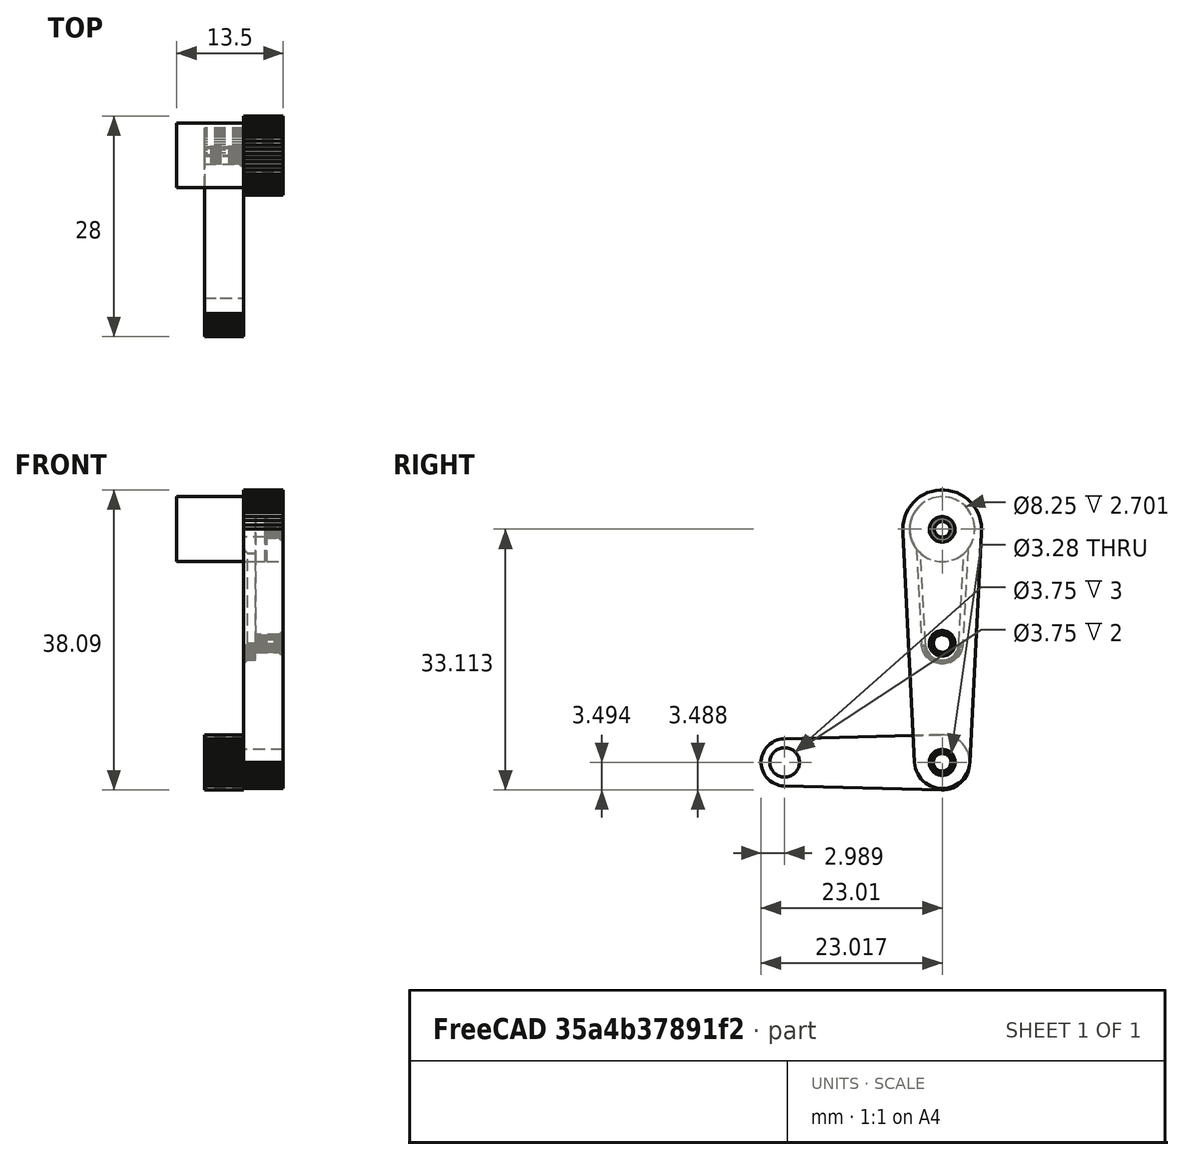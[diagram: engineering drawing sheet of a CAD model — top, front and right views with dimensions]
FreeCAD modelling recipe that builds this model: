
FCSTD DOCUMENT  (FreeCAD 1.0R39109 (Git))
Label: servo-trigger
License: All rights reserved
LicenseURL: https://en.wikipedia.org/wiki/All_rights_reserved
objects: Part::Extrusion×11, Sketcher::SketchObject×7, Part::Cut×6, Mesh::Feature×4, Part::Feature×4, Part::Refine×2, Part::Fuse×2
note: 39 computed .brp shape members not serialized (recipe doc carries the construction recipe); baked Part::Feature solids carry a one-line shape summary decoded from their .brp

FEATURE [Mesh::Feature] trigger_extension  label="trigger-extension"
FEATURE [Mesh::Feature] servo_trigger  label="servo-trigger"
FEATURE [Part::Feature] servo_trigger001
  shape: bbox 5 x 10 x 37.92 mm, 1666 faces, 0 solids (baked)
FEATURE [Part::Refine] servo_trigger002
  Source = -> servo_trigger001
FEATURE [Sketcher::SketchObject] Sketch
  ArcFitTolerance = 1e-06
  AttachmentSupport = -> [servo_trigger002]
  ExternalGeometry = -> [servo_trigger002]
  FullyConstrained = true
  MakeInternals = false
  MapMode = 5
  Placement = pos=(-3,0,0) rot=(0.57735,-0.57735,-0.57735;2.0944rad)
  sketch-geometry (3):
    g0: Circle CenterX=-59.0871 CenterY=190.492 CenterZ=0 NormalX=0 NormalY=0 NormalZ=1 AngleXU=0 Radius=4.125
    g1: LineSegment [constr] StartX=-59.0089 StartY=191.604 StartZ=0 EndX=-59.1307 EndY=189.357 EndZ=0
    g2: LineSegment [constr] StartX=-60.1685 StartY=190.722 StartZ=0 EndX=-58.0037 EndY=190.121 EndZ=0
  constraints (7):
    c: Diameter(g0) = 8.25
    c: Coincident(g1,g-25)
    c: Coincident(g1,g-41)
    c: Coincident(g2,g-33)
    c: Coincident(g2,g-16)
    c: Block(g2)
    c: Block(g0)
FEATURE [Part::Extrusion] Extrude
  Base = -> Sketch
  Dir = (-1,0,0)
  DirMode = 2
  FaceMakerClass = Part::FaceMakerBullseye
  FaceMakerMode = 3
  LengthFwd = 10
  LengthRev = 0
  Solid = true
  Symmetric = false
FEATURE [Part::Extrusion] Extrude001
  Base = -> Sketch
  Dir = (-1,0,0)
  DirMode = 2
  FaceMakerClass = Part::FaceMakerBullseye
  FaceMakerMode = 3
  LengthFwd = 10
  LengthRev = 1.5
  Solid = true
  Symmetric = false
FEATURE [Part::Cut] Cut
  Base = -> servo_trigger002
  Tool = -> Extrude001
FEATURE [Part::Extrusion] Extrude002
  Base = -> Sketch
  Dir = (-1,0,0)
  DirMode = 2
  FaceMakerClass = Part::FaceMakerBullseye
  FaceMakerMode = 3
  LengthFwd = 0
  LengthRev = 2
  Placement = pos=(1.4,0,0) rot=(0,0,1;0rad)
  Solid = true
  Symmetric = false
FEATURE [Sketcher::SketchObject] Sketch001
  ArcFitTolerance = 1e-06
  AttachmentSupport = -> [Cut]
  FullyConstrained = true
  MakeInternals = false
  MapMode = 5
  Placement = pos=(0.5,0,0) rot=(0.57735,0.57735,0.57735;2.0944rad)
  sketch-geometry (2):
    g0: Circle CenterX=59.0881 CenterY=190.477 CenterZ=0 NormalX=0 NormalY=0 NormalZ=1 AngleXU=0 Radius=1
    g1: Circle [constr] CenterX=59.0754 CenterY=190.477 CenterZ=0 NormalX=0 NormalY=0 NormalZ=1 AngleXU=0 Radius=1.61528
  constraints (3):
    c: Diameter(g0) = 2
    c: Block(g1)
    c: Block(g0)
FEATURE [Part::Extrusion] Extrude003
  Base = -> Sketch001
  Dir = (1,0,0)
  DirMode = 2
  FaceMakerClass = Part::FaceMakerBullseye
  FaceMakerMode = 3
  LengthFwd = 0
  LengthRev = 5
  Solid = true
  Symmetric = false
FEATURE [Part::Feature] servo_trigger003_solid  label="servo_trigger003 (Solid)"
  shape: bbox 5 x 10 x 37.92 mm, 1110 faces (baked)
FEATURE [Part::Extrusion] Extrude004
  Base = -> Sketch
  Dir = (-1,0,0)
  DirMode = 2
  FaceMakerClass = Part::FaceMakerBullseye
  FaceMakerMode = 3
  LengthFwd = 10
  LengthRev = 1.2
  Solid = true
  Symmetric = false
FEATURE [Part::Cut] Cut001
  Base = -> servo_trigger003_solid
  Tool = -> Extrude004
FEATURE [Sketcher::SketchObject] Sketch002
  ArcFitTolerance = 1e-06
  AttachmentSupport = -> [Cut001]
  FullyConstrained = true
  MakeInternals = false
  MapMode = 5
  Placement = pos=(0.5,0,0) rot=(0.57735,0.57735,0.57735;2.0944rad)
  sketch-geometry (1):
    g0: Circle CenterX=59.0801 CenterY=160.874 CenterZ=0 NormalX=0 NormalY=0 NormalZ=1 AngleXU=0 Radius=1.64167
  constraints (1):
    c: Block(g0)
FEATURE [Part::Extrusion] Extrude006
  Base = -> Sketch002
  Dir = (1,0,0)
  DirMode = 2
  FaceMakerClass = Part::FaceMakerBullseye
  FaceMakerMode = 3
  LengthFwd = 0
  LengthRev = 5
  Solid = true
  Symmetric = false
FEATURE [Part::Fuse] Fusion
  Base = -> Cut001
  Tool = -> Extrude006
FEATURE [Part::Extrusion] Extrude007
  Base = -> Sketch002
  Dir = (1,0,0)
  DirMode = 2
  FaceMakerClass = Part::FaceMakerBullseye
  FaceMakerMode = 3
  LengthFwd = 0
  LengthRev = 5
  Solid = true
  Symmetric = false
FEATURE [Part::Cut] Cut002
  Base = -> Fusion
  Tool = -> Extrude007
FEATURE [Part::Feature] trigger_extension001
  shape: bbox 5 x 26.5 x 6.998 mm, 904 faces, 0 solids (baked)
FEATURE [Part::Refine] trigger_extension002
  Source = -> trigger_extension001
FEATURE [Part::Feature] trigger_extension002_solid  label="trigger_extension002 (Solid)"
  shape: bbox 5 x 26.5 x 6.998 mm, 529 faces (baked)
FEATURE [Sketcher::SketchObject] Sketch003
  ArcFitTolerance = 1e-06
  AttachmentSupport = -> [trigger_extension002_solid]
  FullyConstrained = true
  MakeInternals = false
  MapMode = 5
  Placement = pos=(-9.5,0,0) rot=(0.57735,-0.57735,-0.57735;2.0944rad)
  sketch-geometry (1):
    g0: Circle CenterX=-39.0698 CenterY=160.877 CenterZ=0 NormalX=0 NormalY=0 NormalZ=1 AngleXU=0 Radius=2.225
  constraints (2):
    c: Diameter(g0) = 4.45
    c: Block(g0)
FEATURE [Part::Extrusion] Extrude008
  Base = -> Sketch003
  Dir = (-1,0,0)
  DirMode = 2
  FaceMakerClass = Part::FaceMakerBullseye
  FaceMakerMode = 3
  LengthFwd = 0
  LengthRev = 5
  Solid = true
  Symmetric = false
FEATURE [Part::Fuse] Fusion001
  Base = -> trigger_extension002_solid
  Tool = -> Extrude008
FEATURE [Sketcher::SketchObject] Sketch004
  ArcFitTolerance = 1e-06
  AttachmentSupport = -> [Fusion001]
  FullyConstrained = true
  MakeInternals = false
  MapMode = 5
  Placement = pos=(-9.5,0,0) rot=(0.57735,-0.57735,-0.57735;2.0944rad)
  sketch-geometry (2):
    g0: Circle [constr] CenterX=-39.0641 CenterY=160.873 CenterZ=0 NormalX=0 NormalY=0 NormalZ=1 AngleXU=0 Radius=2.225
    g1: Circle CenterX=-39.0639 CenterY=160.874 CenterZ=0 NormalX=0 NormalY=0 NormalZ=1 AngleXU=0 Radius=1.5
  constraints (4):
    c: Diameter(g0) = 4.45
    c: Diameter(g1) = 3
    c: Block(g0)
    c: Block(g1)
FEATURE [Part::Extrusion] Extrude009
  Base = -> Sketch004
  Dir = (-1,0,0)
  DirMode = 2
  FaceMakerClass = Part::FaceMakerBullseye
  FaceMakerMode = 3
  LengthFwd = 0
  LengthRev = 3
  Placement = pos=(2.1,0,0) rot=(0,0,1;0rad)
  Solid = true
  Symmetric = false
FEATURE [Part::Cut] Cut003
  Base = -> Fusion001
  Tool = -> Extrude009
FEATURE [Mesh::Feature] Mesh  label="servo-trigger001"
FEATURE [Sketcher::SketchObject] Sketch005
  ArcFitTolerance = 1e-06
  AttachmentSupport = -> [Cut003]
  FullyConstrained = true
  MakeInternals = false
  MapMode = 2
FEATURE [Sketcher::SketchObject] Sketch006
  ArcFitTolerance = 1e-06
  AttachmentSupport = -> [Cut003]
  FullyConstrained = true
  MakeInternals = false
  MapMode = 5
  Placement = pos=(-9.5,0,0) rot=(0.57735,-0.57735,-0.57735;2.0944rad)
  sketch-geometry (1):
    g0: Circle CenterX=-39.0586 CenterY=160.867 CenterZ=0 NormalX=0 NormalY=0 NormalZ=1 AngleXU=0 Radius=1.875
  constraints (2):
    c: Diameter(g0) = 3.75
    c: Block(g0)
FEATURE [Part::Extrusion] Extrude010
  Base = -> Sketch006
  Dir = (-1,0,0)
  DirMode = 2
  FaceMakerClass = Part::FaceMakerBullseye
  FaceMakerMode = 3
  LengthFwd = 0
  LengthRev = 3
  Placement = pos=(2,0,0) rot=(0,0,1;0rad)
  Solid = true
  Symmetric = false
FEATURE [Part::Cut] Cut004
  Base = -> Cut003
  Tool = -> Extrude010
FEATURE [Part::Extrusion] Extrude011
  Base = -> Sketch006
  Dir = (-1,0,0)
  DirMode = 2
  FaceMakerClass = Part::FaceMakerBullseye
  FaceMakerMode = 3
  LengthFwd = 10
  LengthRev = 0
  Solid = true
  Symmetric = true
FEATURE [Part::Cut] Cut005
  Base = -> Cut004
  Tool = -> Extrude011
FEATURE [Mesh::Feature] Mesh001  label="trigger-extension001"
